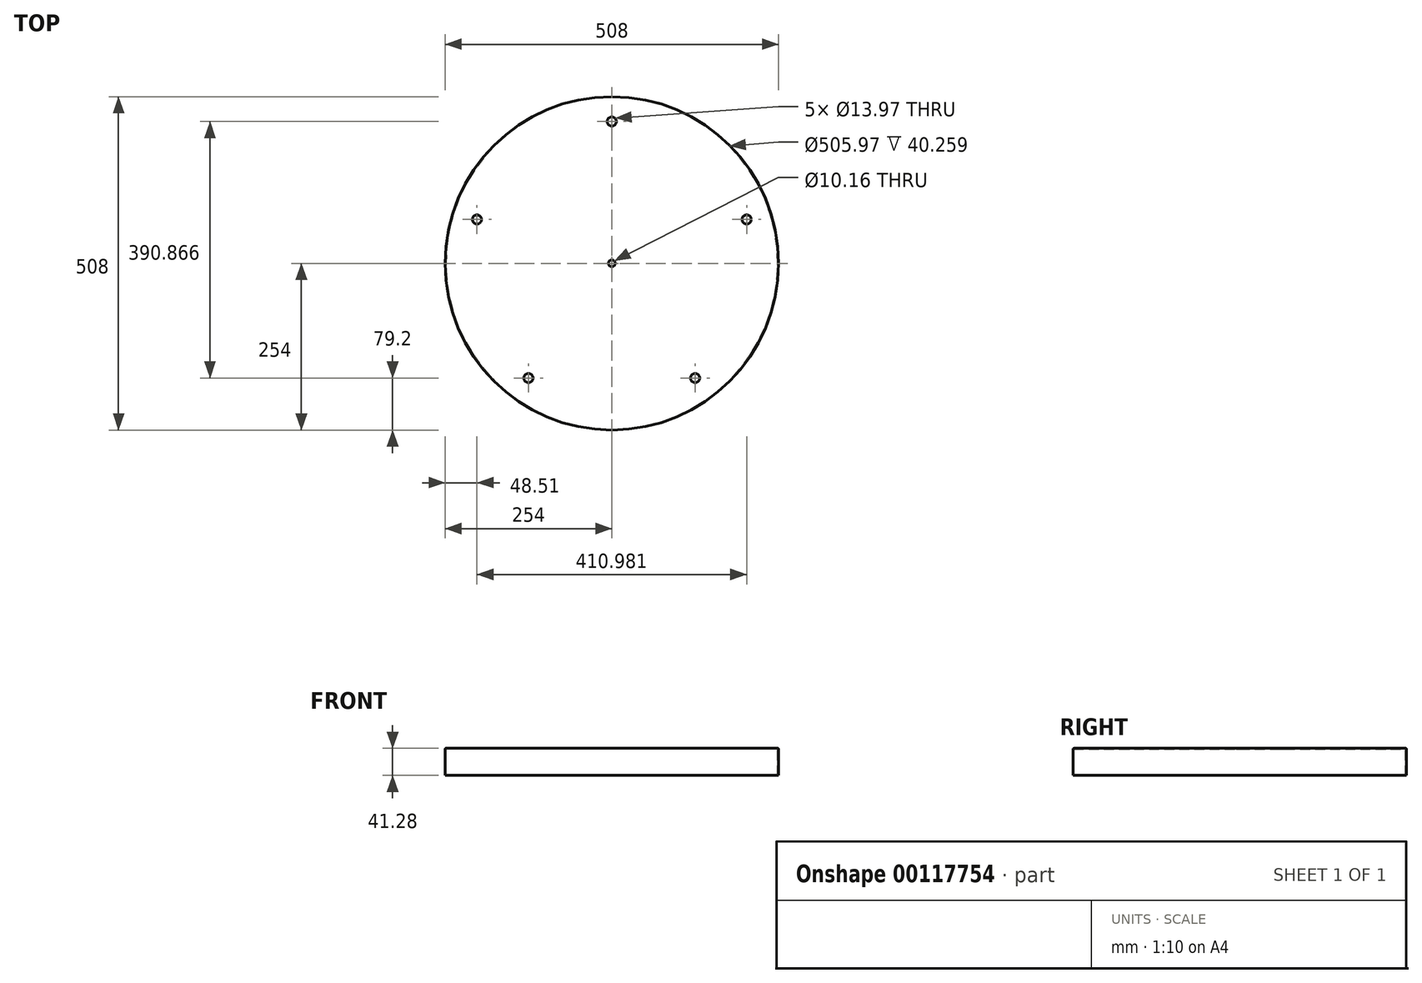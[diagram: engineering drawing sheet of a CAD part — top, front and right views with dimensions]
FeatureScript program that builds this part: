
annotation { "Feature Type Name" : "Feature", "Feature Type Description" : "" }
export const myFeature = defineFeature(function(context is Context, id is Id, definition is map)
    precondition{}
    {
        {
            var Q0;
            Q0=qCreatedBy(makeId("Top.planeOp"),FACE);
            var sketch = newSketch(context, id + "F0", { "sketchPlane" : qUnion([Q0])});
            skCircle(sketch, "E0.cCircle", {"center": v(0, 0) * mm, "radius": 174.8 * mm, "construction": true});
            skLineSegment(sketch, "E0.0", {"start": v(0, 216.07) * mm, "end": v(205.5, 66.77) * mm});
            skLineSegment(sketch, "E0.1", {"start": v(205.5, 66.77) * mm, "end": v(127, -174.8) * mm, "construction": true});
            skLineSegment(sketch, "E0.2", {"start": v(127, -174.8) * mm, "end": v(-127, -174.8) * mm});
            skLineSegment(sketch, "E0.3", {"start": v(-127, -174.8) * mm, "end": v(-205.5, 66.77) * mm});
            skLineSegment(sketch, "E0.4", {"start": v(-205.5, 66.77) * mm, "end": v(0, 216.07) * mm});
            skPoint(sketch, "E0.0.midPoint", {"position": v(102.75, 141.42) * mm});
            skLineSegment(sketch, "E1", {"start": v(0, 0) * mm, "end": v(0, 348.1) * mm, "construction": true});
            skCircle(sketch, "E2", {"center": v(0, 0) * mm, "radius": 254 * mm});
            skLineSegment(sketch, "E3.0", {"start": v(0, 247.46) * mm, "end": v(235.35, 76.47) * mm, "construction": true});
            skLineSegment(sketch, "E3.1", {"start": v(-235.35, 76.47) * mm, "end": v(0, 247.46) * mm, "construction": true});
            skLineSegment(sketch, "E3.2", {"start": v(235.35, 76.47) * mm, "end": v(145.45, -200.2) * mm, "construction": true});
            skLineSegment(sketch, "E3.3", {"start": v(145.45, -200.2) * mm, "end": v(-145.45, -200.2) * mm, "construction": true});
            skLineSegment(sketch, "E3.4", {"start": v(-145.45, -200.2) * mm, "end": v(-235.35, 76.47) * mm, "construction": true});
            skSolve(sketch);
        }
        {
            var Q0;
            Q0=qCreatedBy(makeId("Front.planeOp"),FACE);
            var sketch = newSketch(context, id + "F1", { "sketchPlane" : qUnion([Q0])});
            skLineSegment(sketch, "E4.0", {"start": v(0, 0) * mm, "end": v(252.48, 0) * mm});
            skLineSegment(sketch, "E5", {"start": v(254, -1.52) * mm, "end": v(254, -41.28) * mm});
            skLineSegment(sketch, "E6", {"start": v(0, 0) * mm, "end": v(0, -88.14) * mm, "construction": true});
            skLineSegment(sketch, "E7.0", {"start": v(252.98, -1.02) * mm, "end": v(252.98, -41.28) * mm});
            skLineSegment(sketch, "E7.1", {"start": v(0, -1.02) * mm, "end": v(252.98, -1.02) * mm});
            skLineSegment(sketch, "E8", {"start": v(254, -41.28) * mm, "end": v(252.98, -41.28) * mm});
            skPoint(sketch, "E9.visualSharp", {"position": v(254, 0) * mm});
            skArc(sketch, "E9.filletArc", {"start": v(254, -1.52) * mm, "mid": v(253.55, -0.45) * mm, "end": v(252.48, 0) * mm});
            skLineSegment(sketch, "E10", {"start": v(0, 0) * mm, "end": v(0, -1.02) * mm});
            skSolve(sketch);
        }
        {
            var Q0;
            Q0 = qSketchRegion(id + "F1", true);
            var Q1;
            Q1=sQuery(id+"F1.wireOp",EDGE,"E6");
            revolve(context, id + "F2", {"entities" : qUnion([Q0]), "axis" : qUnion([Q1]), "revolveType" : RevolveType.FULL});
        }
        {
            var Q0;
            Q0=qCreatedBy(makeId("Top.planeOp"),FACE);
            var sketch = newSketch(context, id + "F3", { "sketchPlane" : qUnion([Q0])});
            skCircle(sketch, "E11.0", {"center": v(0, 0) * mm, "radius": 174.8 * mm, "construction": true});
            skLineSegment(sketch, "E11.1", {"start": v(0, 216.07) * mm, "end": v(205.5, 66.77) * mm, "construction": true});
            skLineSegment(sketch, "E11.2", {"start": v(205.5, 66.77) * mm, "end": v(127, -174.8) * mm, "construction": true});
            skLineSegment(sketch, "E11.3", {"start": v(127, -174.8) * mm, "end": v(-127, -174.8) * mm, "construction": true});
            skLineSegment(sketch, "E11.4", {"start": v(-127, -174.8) * mm, "end": v(-205.5, 66.77) * mm, "construction": true});
            skLineSegment(sketch, "E11.5", {"start": v(-205.5, 66.77) * mm, "end": v(0, 216.07) * mm, "construction": true});
            skPoint(sketch, "E11.6", {"position": v(102.75, 141.42) * mm});
            skLineSegment(sketch, "E11.7", {"start": v(0, 0) * mm, "end": v(0, 348.1) * mm, "construction": true});
            skCircle(sketch, "E11.8", {"center": v(0, 0) * mm, "radius": 254 * mm, "construction": true});
            skLineSegment(sketch, "E11.9", {"start": v(0, 247.46) * mm, "end": v(235.35, 76.47) * mm, "construction": true});
            skLineSegment(sketch, "E11.10", {"start": v(-235.35, 76.47) * mm, "end": v(0, 247.46) * mm, "construction": true});
            skLineSegment(sketch, "E11.11", {"start": v(235.35, 76.47) * mm, "end": v(145.45, -200.2) * mm, "construction": true});
            skLineSegment(sketch, "E11.12", {"start": v(145.45, -200.2) * mm, "end": v(-145.45, -200.2) * mm, "construction": true});
            skLineSegment(sketch, "E11.13", {"start": v(-145.45, -200.2) * mm, "end": v(-235.35, 76.47) * mm, "construction": true});
            skCircle(sketch, "E11.14", {"center": v(0, 0) * mm, "radius": 254 * mm, "construction": true});
            skCircle(sketch, "E12", {"center": v(205.5, 66.77) * mm, "radius": 6.99 * mm});
            skCircle(sketch, "E13", {"center": v(0, 216.07) * mm, "radius": 6.99 * mm});
            skCircle(sketch, "E14", {"center": v(-205.5, 66.77) * mm, "radius": 6.99 * mm});
            skCircle(sketch, "E15", {"center": v(-127, -174.8) * mm, "radius": 6.99 * mm});
            skCircle(sketch, "E16", {"center": v(127, -174.8) * mm, "radius": 6.99 * mm});
            skCircle(sketch, "E17", {"center": v(0, 0) * mm, "radius": 5.08 * mm});
            skSolve(sketch);
        }
        {
            var Q0;
            Q0 = qSketchRegion(id + "F3", true);
            var Q1;
            Q1=makeQuery(id+"F2.opRevolve","SWEPT_FACE",FACE,{"disambiguationData":[OSD([sQuery(id+"F1.wireOp",EDGE,"E7.1")])]});
            extrude(context, id + "F4", {"entities" : qUnion([Q0]), "operationType" : NewBodyOperationType.REMOVE, "endBound" : BoundingType.UP_TO_SURFACE, "oppositeDirection" : true, "endBoundEntityFace" : qUnion([Q1]), "depth" : 25.4 * mm});
        }
    });
